annotation { "Feature Type Name" : "Feature", "Feature Type Description" : "" }
export const myFeature = defineFeature(function(context is Context, id is Id, definition is map)
    precondition{}
    {
        {
            var Q0;
            Q0=qCreatedBy(makeId("Top.planeOp"),FACE);
            var sketch = newSketch(context, id + "F0", { "sketchPlane" : qUnion([Q0])});
            skLineSegment(sketch, "E0.bottom", {"start": v(46, -17.5) * mm, "end": v(-44, -17.5) * mm});
            skLineSegment(sketch, "E0.top", {"start": v(46, 20.5) * mm, "end": v(-44, 20.5) * mm});
            skLineSegment(sketch, "E0.left", {"start": v(46, -17.5) * mm, "end": v(46, 20.5) * mm});
            skLineSegment(sketch, "E0.right", {"start": v(-44, -17.5) * mm, "end": v(-44, 20.5) * mm});
            skSolve(sketch);
        }
        {
            var Q0;
            Q0=qSketchRegion(id+"F0",true);
            extrude(context, id + "F1", {"entities" : qUnion([Q0]), "depth" : 1.5 * mm, "offsetDistance" : 25 * mm});
        }
        {
            var Q0;
            Q0=makeQuery(id+"F1.opExtrude","CAP_FACE",FACE,{"disambiguationData":[OSD([sQuery(id+"F0.wireOp",EDGE,"E0.bottom"),sQuery(id+"F0.wireOp",EDGE,"E0.top"),sQuery(id+"F0.wireOp",EDGE,"E0.left"),sQuery(id+"F0.wireOp",EDGE,"E0.right")])],"isStart":false});
            var sketch = newSketch(context, id + "F2", { "sketchPlane" : qUnion([Q0])});
            skLineSegment(sketch, "E1.bottom", {"start": v(-40.5, 17) * mm, "end": v(42.5, 17) * mm});
            skLineSegment(sketch, "E1.top", {"start": v(-40.5, -14) * mm, "end": v(42.5, -14) * mm});
            skLineSegment(sketch, "E1.left", {"start": v(-40.5, 17) * mm, "end": v(-40.5, -14) * mm});
            skLineSegment(sketch, "E1.right", {"start": v(42.5, 17) * mm, "end": v(42.5, -14) * mm});
            skLineSegment(sketch, "E2.bottom", {"start": v(-44, 20.5) * mm, "end": v(46, 20.5) * mm});
            skLineSegment(sketch, "E2.top", {"start": v(-44, -17.5) * mm, "end": v(46, -17.5) * mm});
            skLineSegment(sketch, "E2.left", {"start": v(-44, 20.5) * mm, "end": v(-44, -17.5) * mm});
            skLineSegment(sketch, "E2.right", {"start": v(46, 20.5) * mm, "end": v(46, -17.5) * mm});
            skSolve(sketch);
        }
        {
            var Q0;
            Q0=qSketchRegion(id+"F2",true);
            extrude(context, id + "F3", {"entities" : qUnion([Q0]), "operationType" : NewBodyOperationType.ADD, "depth" : 3 * mm});
        }
        {
            var Q0;
            Q0=makeQuery(id+"F3.boolean.opBoolean","MERGE",EDGE,{"derivedFrom":[makeQuery(id+"F1.opExtrude","SWEPT_EDGE",EDGE,{"disambiguationData":[OSD([sQuery(id+"F0.wireOp",EDGE,"E0.top"),sQuery(id+"F0.wireOp",EDGE,"E0.right")])]}),makeQuery(id+"F3.opExtrude","SWEPT_EDGE",EDGE,{"disambiguationData":[OSD([sQuery(id+"F2.wireOp",EDGE,"E2.bottom"),sQuery(id+"F2.wireOp",EDGE,"E2.left")])]})]});
            var Q1;
            Q1=makeQuery(id+"F3.boolean.opBoolean","MERGE",EDGE,{"derivedFrom":[makeQuery(id+"F1.opExtrude","SWEPT_EDGE",EDGE,{"disambiguationData":[OSD([sQuery(id+"F0.wireOp",EDGE,"E0.top"),sQuery(id+"F0.wireOp",EDGE,"E0.left")])]}),makeQuery(id+"F3.opExtrude","SWEPT_EDGE",EDGE,{"disambiguationData":[OSD([sQuery(id+"F2.wireOp",EDGE,"E2.bottom"),sQuery(id+"F2.wireOp",EDGE,"E2.right")])]})]});
            var Q2;
            Q2=makeQuery(id+"F3.boolean.opBoolean","MERGE",EDGE,{"derivedFrom":[makeQuery(id+"F1.opExtrude","SWEPT_EDGE",EDGE,{"disambiguationData":[OSD([sQuery(id+"F0.wireOp",EDGE,"E0.bottom"),sQuery(id+"F0.wireOp",EDGE,"E0.left")])]}),makeQuery(id+"F3.opExtrude","SWEPT_EDGE",EDGE,{"disambiguationData":[OSD([sQuery(id+"F2.wireOp",EDGE,"E2.top"),sQuery(id+"F2.wireOp",EDGE,"E2.right")])]})]});
            var Q3;
            Q3=makeQuery(id+"F3.boolean.opBoolean","MERGE",EDGE,{"derivedFrom":[makeQuery(id+"F1.opExtrude","SWEPT_EDGE",EDGE,{"disambiguationData":[OSD([sQuery(id+"F0.wireOp",EDGE,"E0.bottom"),sQuery(id+"F0.wireOp",EDGE,"E0.right")])]}),makeQuery(id+"F3.opExtrude","SWEPT_EDGE",EDGE,{"disambiguationData":[OSD([sQuery(id+"F2.wireOp",EDGE,"E2.top"),sQuery(id+"F2.wireOp",EDGE,"E2.left")])]})]});
            fillet(context, id + "F4", {"entities" : qUnion([Q0, Q1, Q2, Q3]), "radius" : 3 * mm, "tangentPropagation" : true, "allowEdgeOverflow" : false});
        }
        {
            var Q0;
            Q0=makeQuery(id+"F3.opExtrude","CAP_FACE",FACE,{"disambiguationData":[OSD([sQuery(id+"F2.wireOp",EDGE,"E1.bottom"),sQuery(id+"F2.wireOp",EDGE,"E1.top"),sQuery(id+"F2.wireOp",EDGE,"E1.left"),sQuery(id+"F2.wireOp",EDGE,"E1.right"),sQuery(id+"F2.wireOp",EDGE,"E2.bottom"),sQuery(id+"F2.wireOp",EDGE,"E2.top"),sQuery(id+"F2.wireOp",EDGE,"E2.left"),sQuery(id+"F2.wireOp",EDGE,"E2.right")])],"isStart":false});
            var sketch = newSketch(context, id + "F5", { "sketchPlane" : qUnion([Q0])});
            skLineSegment(sketch, "E3.bottom", {"start": v(-41.8, 18.3) * mm, "end": v(43.8, 18.3) * mm});
            skLineSegment(sketch, "E3.top", {"start": v(-41.8, -15.3) * mm, "end": v(43.8, -15.3) * mm});
            skLineSegment(sketch, "E3.left", {"start": v(-41.8, 18.3) * mm, "end": v(-41.8, -15.3) * mm});
            skLineSegment(sketch, "E3.right", {"start": v(43.8, 18.3) * mm, "end": v(43.8, -15.3) * mm});
            skLineSegment(sketch, "E4.bottom", {"start": v(-42.3, 18.8) * mm, "end": v(44.3, 18.8) * mm});
            skLineSegment(sketch, "E4.top", {"start": v(-42.3, -15.8) * mm, "end": v(44.3, -15.8) * mm});
            skLineSegment(sketch, "E4.left", {"start": v(-42.3, 18.8) * mm, "end": v(-42.3, -15.8) * mm});
            skLineSegment(sketch, "E4.right", {"start": v(44.3, 18.8) * mm, "end": v(44.3, -15.8) * mm});
            skSolve(sketch);
        }
        {
            var Q0;
            Q0=qSketchRegion(id+"F5",true);
            extrude(context, id + "F6", {"entities" : qUnion([Q0]), "operationType" : NewBodyOperationType.ADD, "depth" : 2 * mm, "offsetDistance" : 25 * mm});
        }
        {
            var Q0;
            Q0=makeQuery(id+"F1.opExtrude","CAP_FACE",FACE,{"disambiguationData":[OSD([sQuery(id+"F0.wireOp",EDGE,"E0.bottom"),sQuery(id+"F0.wireOp",EDGE,"E0.top"),sQuery(id+"F0.wireOp",EDGE,"E0.left"),sQuery(id+"F0.wireOp",EDGE,"E0.right")])],"isStart":true});
            var sketch = newSketch(context, id + "F7", { "sketchPlane" : qUnion([Q0])});
            skText(sketch, "E5", { "text": "GPS ROM", "fontName": "AllertaStencil-Regular.ttf"});
            const initialGuessF7  = {"E5": [-0.03, 0.00194, 1, 0, 0.01106]};
            skSetInitialGuess(sketch, initialGuessF7);
            skSolve(sketch);
        }
        {
            var Q0;
            Q0=qSketchRegion(id+"F7",true);
            extrude(context, id + "F8", {"entities" : qUnion([Q0]), "operationType" : NewBodyOperationType.REMOVE, "oppositeDirection" : true, "depth" : 1 * mm, "offsetDistance" : 25 * mm});
        }
        {
            var Q0;
            Q0=makeQuery(id+"F1.opExtrude","CAP_FACE",FACE,{"disambiguationData":[OSD([sQuery(id+"F0.wireOp",EDGE,"E0.bottom"),sQuery(id+"F0.wireOp",EDGE,"E0.top"),sQuery(id+"F0.wireOp",EDGE,"E0.left"),sQuery(id+"F0.wireOp",EDGE,"E0.right")])],"isStart":false});
            var sketch = newSketch(context, id + "F9", { "sketchPlane" : qUnion([Q0])});
            skCircle(sketch, "E6", {"center": v(0, 10.5) * mm, "radius": 2.5 * mm});
            skSolve(sketch);
        }
        {
            var Q0;
            Q0=qSketchRegion(id+"F9",true);
            extrude(context, id + "F10", {"entities" : qUnion([Q0]), "operationType" : NewBodyOperationType.ADD, "depth" : 9.5 * mm, "offsetDistance" : 25 * mm});
        }
        {
            var Q0;
            Q0=makeQuery(id+"F1.opExtrude","CAP_FACE",FACE,{"disambiguationData":[OSD([sQuery(id+"F0.wireOp",EDGE,"E0.bottom"),sQuery(id+"F0.wireOp",EDGE,"E0.top"),sQuery(id+"F0.wireOp",EDGE,"E0.left"),sQuery(id+"F0.wireOp",EDGE,"E0.right")])],"isStart":false});
            var sketch = newSketch(context, id + "F11", { "sketchPlane" : qUnion([Q0])});
            skCircle(sketch, "E7", {"center": v(0, 10.5) * mm, "radius": 5.5 * mm});
            skLineSegment(sketch, "E8.bottom", {"start": v(-30, 17) * mm, "end": v(40, 17) * mm});
            skLineSegment(sketch, "E8.top", {"start": v(-30, 1) * mm, "end": v(40, 1) * mm});
            skLineSegment(sketch, "E8.left", {"start": v(-30, 17) * mm, "end": v(-30, 1) * mm});
            skLineSegment(sketch, "E8.right", {"start": v(40, 17) * mm, "end": v(40, 1) * mm});
            skSolve(sketch);
        }
        {
            var Q0;
            Q0=qSketchRegion(id+"F11",true);
            extrude(context, id + "F12", {"entities" : qUnion([Q0]), "operationType" : NewBodyOperationType.REMOVE, "oppositeDirection" : true, "depth" : 1 * mm, "offsetDistance" : 25 * mm});
        }
        {
            var Q0;
            Q0=makeQuery(id+"F1.opExtrude","CAP_FACE",FACE,{"disambiguationData":[OSD([sQuery(id+"F0.wireOp",EDGE,"E0.bottom"),sQuery(id+"F0.wireOp",EDGE,"E0.top"),sQuery(id+"F0.wireOp",EDGE,"E0.left"),sQuery(id+"F0.wireOp",EDGE,"E0.right")])],"isStart":false});
            var sketch = newSketch(context, id + "F13", { "sketchPlane" : qUnion([Q0])});
            skLineSegment(sketch, "E9.bottom", {"start": v(-39.3, 11.7) * mm, "end": v(-35.8, 11.7) * mm});
            skLineSegment(sketch, "E9.top", {"start": v(-39.3, 6.7) * mm, "end": v(-35.8, 6.7) * mm});
            skLineSegment(sketch, "E9.left", {"start": v(-39.3, 11.7) * mm, "end": v(-39.3, 6.7) * mm});
            skLineSegment(sketch, "E9.right", {"start": v(-35.8, 11.7) * mm, "end": v(-35.8, 6.7) * mm});
            skLineSegment(sketch, "E10", {"start": v(-40.5, 1.5) * mm, "end": v(42.5, 1.5) * mm, "construction": true});
            skLineSegment(sketch, "E11.MirrorCS", {"start": v(-39.3, -8.7) * mm, "end": v(-35.8, -8.7) * mm});
            skLineSegment(sketch, "E12.MirrorCS", {"start": v(-35.8, -8.7) * mm, "end": v(-35.8, -3.7) * mm});
            skLineSegment(sketch, "E13.MirrorCS", {"start": v(-39.3, -3.7) * mm, "end": v(-35.8, -3.7) * mm});
            skLineSegment(sketch, "E14.MirrorCS", {"start": v(-39.3, -8.7) * mm, "end": v(-39.3, -3.7) * mm});
            skSolve(sketch);
        }
        {
            var Q0;
            Q0=qSketchRegion(id+"F13",true);
            extrude(context, id + "F14", {"entities" : qUnion([Q0]), "operationType" : NewBodyOperationType.REMOVE, "oppositeDirection" : true, "depth" : 1.3 * mm, "offsetDistance" : 25 * mm});
        }
        {
            var Q0;
            Q0=makeQuery(id+"F6.opExtrude","SWEPT_EDGE",EDGE,{"disambiguationData":[OSD([sQuery(id+"F5.wireOp",EDGE,"E4.bottom"),sQuery(id+"F5.wireOp",EDGE,"E4.right")])]});
            var Q1;
            Q1=makeQuery(id+"F6.opExtrude","SWEPT_EDGE",EDGE,{"disambiguationData":[OSD([sQuery(id+"F5.wireOp",EDGE,"E4.top"),sQuery(id+"F5.wireOp",EDGE,"E4.right")])]});
            var Q2;
            Q2=makeQuery(id+"F6.opExtrude","SWEPT_EDGE",EDGE,{"disambiguationData":[OSD([sQuery(id+"F5.wireOp",EDGE,"E4.top"),sQuery(id+"F5.wireOp",EDGE,"E4.left")])]});
            var Q3;
            Q3=makeQuery(id+"F6.opExtrude","SWEPT_EDGE",EDGE,{"disambiguationData":[OSD([sQuery(id+"F5.wireOp",EDGE,"E4.bottom"),sQuery(id+"F5.wireOp",EDGE,"E4.left")])]});
            var Q4;
            Q4=makeQuery(id+"F6.opExtrude","SWEPT_EDGE",EDGE,{"disambiguationData":[OSD([sQuery(id+"F5.wireOp",EDGE,"E3.top"),sQuery(id+"F5.wireOp",EDGE,"E3.left")])]});
            var Q5;
            Q5=makeQuery(id+"F6.opExtrude","SWEPT_EDGE",EDGE,{"disambiguationData":[OSD([sQuery(id+"F5.wireOp",EDGE,"E3.bottom"),sQuery(id+"F5.wireOp",EDGE,"E3.left")])]});
            var Q6;
            Q6=makeQuery(id+"F6.opExtrude","SWEPT_EDGE",EDGE,{"disambiguationData":[OSD([sQuery(id+"F5.wireOp",EDGE,"E3.top"),sQuery(id+"F5.wireOp",EDGE,"E3.right")])]});
            var Q7;
            Q7=makeQuery(id+"F6.opExtrude","SWEPT_EDGE",EDGE,{"disambiguationData":[OSD([sQuery(id+"F5.wireOp",EDGE,"E3.bottom"),sQuery(id+"F5.wireOp",EDGE,"E3.right")])]});
            fillet(context, id + "F15", {"entities" : qUnion([Q0, Q1, Q2, Q3, Q4, Q5, Q6, Q7]), "radius" : 1.5 * mm, "tangentPropagation" : true, "allowEdgeOverflow" : false});
        }
        {
            var Q0;
            Q0=makeQuery(id+"F1.opExtrude","CAP_FACE",FACE,{"disambiguationData":[OSD([sQuery(id+"F0.wireOp",EDGE,"E0.bottom"),sQuery(id+"F0.wireOp",EDGE,"E0.top"),sQuery(id+"F0.wireOp",EDGE,"E0.left"),sQuery(id+"F0.wireOp",EDGE,"E0.right")])],"isStart":true});
            var sketch = newSketch(context, id + "F16", { "sketchPlane" : qUnion([Q0])});
            skPoint(sketch, "E15", {"position": v(0.25, -10.5) * mm});
            skLineSegment(sketch, "E16.bottom", {"start": v(-3.75, -6.5) * mm, "end": v(4.25, -6.5) * mm, "construction": true});
            skLineSegment(sketch, "E16.top", {"start": v(-3.75, -14.5) * mm, "end": v(4.25, -14.5) * mm, "construction": true});
            skLineSegment(sketch, "E16.left", {"start": v(-3.75, -6.5) * mm, "end": v(-3.75, -14.5) * mm, "construction": true});
            skLineSegment(sketch, "E16.right", {"start": v(4.25, -6.5) * mm, "end": v(4.25, -14.5) * mm, "construction": true});
            skLineSegment(sketch, "E17", {"start": v(-3.75, -8.5) * mm, "end": v(4.25, -8.5) * mm, "construction": true});
            skArc(sketch, "E18", {"start": v(-1.25, -8.5) * mm, "mid": v(0.25, -14.1) * mm, "end": v(1.75, -8.5) * mm});
            skLineSegment(sketch, "E19", {"start": v(-1.25, -8.5) * mm, "end": v(-1.75, -7.63) * mm, "construction": true});
            skLineSegment(sketch, "E20", {"start": v(1.75, -8.5) * mm, "end": v(2.25, -7.63) * mm, "construction": true});
            skArc(sketch, "E21", {"start": v(-1.75, -7.63) * mm, "mid": v(0.25, -15.1) * mm, "end": v(2.25, -7.63) * mm});
            skArc(sketch, "E22", {"start": v(-1.25, -8.5) * mm, "mid": v(-1.07, -7.82) * mm, "end": v(-1.75, -7.63) * mm});
            skArc(sketch, "E23", {"start": v(2.25, -7.63) * mm, "mid": v(1.57, -7.82) * mm, "end": v(1.75, -8.5) * mm});
            skLineSegment(sketch, "E24.bottom", {"start": v(-0.25, -6.5) * mm, "end": v(0.75, -6.5) * mm, "construction": true});
            skLineSegment(sketch, "E24.top", {"start": v(-0.25, -11.5) * mm, "end": v(0.75, -11.5) * mm, "construction": true});
            skLineSegment(sketch, "E24.left", {"start": v(-0.25, -6.5) * mm, "end": v(-0.25, -11.5) * mm});
            skLineSegment(sketch, "E24.right", {"start": v(0.75, -6.5) * mm, "end": v(0.75, -11.5) * mm});
            skArc(sketch, "E25", {"start": v(-0.25, -11.5) * mm, "mid": v(0.25, -12) * mm, "end": v(0.75, -11.5) * mm});
            skArc(sketch, "E26", {"start": v(0.75, -6.5) * mm, "mid": v(0.25, -6) * mm, "end": v(-0.25, -6.5) * mm});
            skSolve(sketch);
        }
        {
            var Q0;
            Q0=qSketchRegion(id+"F16",true);
            extrude(context, id + "F17", {"entities" : qUnion([Q0]), "operationType" : NewBodyOperationType.REMOVE, "oppositeDirection" : true, "depth" : 1 * mm, "offsetDistance" : 25 * mm});
        }
        {
            var Q0;
            {var subQ0=makeQuery(id+"F3.opExtrude","SWEPT_FACE",FACE,{"disambiguationData":[OSD([sQuery(id+"F2.wireOp",EDGE,"E1.bottom")])]});Q0=makeQuery(id+"F21.boolean.opBoolean","SPLIT",FACE,{"disambiguationData":[TD([makeQuery(id+"F14.boolean.opBoolean","COPY",FACE,{"derivedFrom":makeQuery(id+"F14.opExtrude","SWEPT_FACE",FACE,{"disambiguationData":[OSD([sQuery(id+"F13.wireOp",EDGE,"E9.bottom")])]})})])],"derivedFrom":makeQuery(id+"F12.boolean.opBoolean","SPLIT",FACE,{"disambiguationData":[TD([subQ0])],"derivedFrom":makeQuery(id+"F1.opExtrude","CAP_FACE",FACE,{"disambiguationData":[OSD([sQuery(id+"F0.wireOp",EDGE,"E0.bottom"),sQuery(id+"F0.wireOp",EDGE,"E0.top"),sQuery(id+"F0.wireOp",EDGE,"E0.left"),sQuery(id+"F0.wireOp",EDGE,"E0.right")])],"isStart":false})})});}
            var sketch = newSketch(context, id + "F18", { "sketchPlane" : qUnion([Q0])});
            skLineSegment(sketch, "E27.bottom", {"start": v(-33.8, 4) * mm, "end": v(-31.5, 4) * mm});
            skLineSegment(sketch, "E27.top", {"start": v(-33.8, 0) * mm, "end": v(-31.5, 0) * mm});
            skLineSegment(sketch, "E27.left", {"start": v(-33.8, 4) * mm, "end": v(-33.8, 0) * mm});
            skLineSegment(sketch, "E27.right", {"start": v(-31.5, 4) * mm, "end": v(-31.5, 0) * mm});
            skLineSegment(sketch, "E28", {"start": v(-35.32, 0) * mm, "end": v(-32.55, 0) * mm, "construction": true});
            skLineSegment(sketch, "E29.MirrorCS", {"start": v(-33.8, -4) * mm, "end": v(-33.8, 0) * mm});
            skLineSegment(sketch, "E30.MirrorCS", {"start": v(-33.8, -4) * mm, "end": v(-31.5, -4) * mm});
            skLineSegment(sketch, "E31.MirrorCS", {"start": v(-31.5, -4) * mm, "end": v(-31.5, 0) * mm});
            skSolve(sketch);
        }
        {
            var Q0;
            Q0=qSketchRegion(id+"F18",true);
            extrude(context, id + "F19", {"entities" : qUnion([Q0]), "operationType" : NewBodyOperationType.REMOVE, "oppositeDirection" : true, "depth" : 1.3 * mm, "offsetDistance" : 25 * mm});
        }
        {
            var Q0;
            Q0=makeQuery(id+"F12.boolean.opBoolean","SPLIT",FACE,{"disambiguationData":[TD([makeQuery(id+"F3.opExtrude","SWEPT_FACE",FACE,{"disambiguationData":[OSD([sQuery(id+"F2.wireOp",EDGE,"E1.bottom")])]})])],"derivedFrom":makeQuery(id+"F1.opExtrude","CAP_FACE",FACE,{"disambiguationData":[OSD([sQuery(id+"F0.wireOp",EDGE,"E0.bottom"),sQuery(id+"F0.wireOp",EDGE,"E0.top"),sQuery(id+"F0.wireOp",EDGE,"E0.left"),sQuery(id+"F0.wireOp",EDGE,"E0.right")])],"isStart":false})});
            var sketch = newSketch(context, id + "F20", { "sketchPlane" : qUnion([Q0])});
            skLineSegment(sketch, "E32.bottom", {"start": v(-31.5, 17) * mm, "end": v(-30, 17) * mm});
            skLineSegment(sketch, "E32.top", {"start": v(-31.5, -14) * mm, "end": v(-30, -14) * mm});
            skLineSegment(sketch, "E32.right", {"start": v(-30, 17) * mm, "end": v(-30, -14) * mm});
            skLineSegment(sketch, "E33.left", {"start": v(-40.5, 1) * mm, "end": v(-40.5, -1) * mm});
            skLineSegment(sketch, "E34", {"start": v(-31.5, 17) * mm, "end": v(-31.5, 5.5) * mm});
            skLineSegment(sketch, "E35", {"start": v(-31.5, 5.5) * mm, "end": v(-35.3, 5.5) * mm});
            skLineSegment(sketch, "E36", {"start": v(-35.3, 5.5) * mm, "end": v(-35.3, 1) * mm});
            skLineSegment(sketch, "E37", {"start": v(-35.3, 1) * mm, "end": v(-40.5, 1) * mm});
            skLineSegment(sketch, "E38.MirrorCS", {"start": v(-31.5, -5.5) * mm, "end": v(-35.3, -5.5) * mm});
            skLineSegment(sketch, "E39.MirrorCS", {"start": v(-35.3, -5.5) * mm, "end": v(-35.3, -1) * mm});
            skLineSegment(sketch, "E40.MirrorCS", {"start": v(-35.3, -1) * mm, "end": v(-40.5, -1) * mm});
            skLineSegment(sketch, "E41", {"start": v(-31.5, 4) * mm, "end": v(-33.8, 4) * mm});
            skLineSegment(sketch, "E42", {"start": v(-33.8, 4) * mm, "end": v(-33.8, -4) * mm});
            skLineSegment(sketch, "E43", {"start": v(-33.8, -4) * mm, "end": v(-31.5, -4) * mm});
            skLineSegment(sketch, "E44", {"start": v(-31.5, -4) * mm, "end": v(-31.5, 4) * mm});
            skLineSegment(sketch, "E45", {"start": v(-31.5, -5.5) * mm, "end": v(-31.5, -14) * mm});
            skSolve(sketch);
        }
        {
            var Q0;
            Q0=qSketchRegion(id+"F20",true);
            extrude(context, id + "F21", {"entities" : qUnion([Q0]), "operationType" : NewBodyOperationType.ADD, "depth" : 8 * mm, "offsetDistance" : 25 * mm});
        }
    });